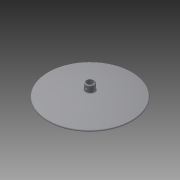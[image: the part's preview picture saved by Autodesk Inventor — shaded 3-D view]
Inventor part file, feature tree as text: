
AUTODESK INVENTOR PART (.ipt)
format: ipt  version: 2014 (Build 180170000, 170)  size: 140,288 bytes
history: native  units: in
note: dims shown in document units (in); Inventor stores cm internally (conversion verified against a paired STEP export)
features: fillet x3, sketch x3, plane x2, extrude x2, revolve x1
ambient origin geometry x8: Origin, YZ Plane, XZ Plane, XY Plane, X Axis, Y Axis, Z Axis, Center Point
bodies: Solid1 (feature_tree)
feature tree (11):
  revolve  "Revolution1"  [1 undecoded]
  fillet  "Fillet1"  Radius=0.25in
  fillet  "Fillet2"  [1 undecoded]
  plane  "Work Plane1"
  extrude  "Extrusion1"  Depth=0.0625in
  plane  "Work Plane2"
  fillet  "Fillet3"  Radius=0.5in
  extrude  "Extrusion2"  Depth=0.0625in TaperAngle=0.0deg
  sketch  "Sketch1"  dims[d0=24.0in d1=11.75in d2=0.25in d3=90.0deg]
  sketch  "Sketch2"  dims[d4=5.0in d5=0.0625in d6=0.5in]
  sketch  "Sketch3"  dims[d7=0.625in d8=0.5in d9=0.1in d10=0.0in d11=0.0in d12=0.125in d13=12.5in d14=1.0in d15=0.0in d16=0.0625in]
note: 2 required parameter values undecoded (feature->parameter linkage not recoverable at this tier; creation-order binding heuristic only, values carry confidence <= 0.55)